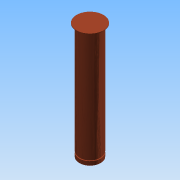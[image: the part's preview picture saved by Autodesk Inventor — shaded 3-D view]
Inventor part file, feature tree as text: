
AUTODESK INVENTOR PART (.ipt)
format: ipt  version: 2015 (Build 190159000, 159)  size: 103,936 bytes
history: native  units: mm
features: sketch x3, extrude x2, revolve x1, chamfer x1
ambient origin geometry x8: Origin, YZ Plane, XZ Plane, XY Plane, X Axis, Y Axis, Z Axis, Center Point
bodies: 实体1 (feature_tree)
feature tree (7):
  extrude  "拉伸1"  Depth=108.34mm TaperAngle=0.0deg
  extrude  "拉伸2"  Depth=0.6mm TaperAngle=0.0deg
  revolve  "旋转1"  [1 undecoded]
  chamfer  "倒角1"  Distance=4.0mm
  sketch  "草图1"  dims[d0=20.0mm d1=108.34mm d2=0.0mm]
  sketch  "草图2"  dims[d3=25.0mm d4=0.6mm d5=0.0mm]
  sketch  "草图3"  dims[d6=10.722393mm d7=1.2mm d8=4.0mm d9=9.175mm d10=6.152985mm d11=90.0deg d12=0.5mm d13=2.0mm d14=45.0deg]
note: 1 required parameter value undecoded (feature->parameter linkage not recoverable at this tier; creation-order binding heuristic only, values carry confidence <= 0.55)
